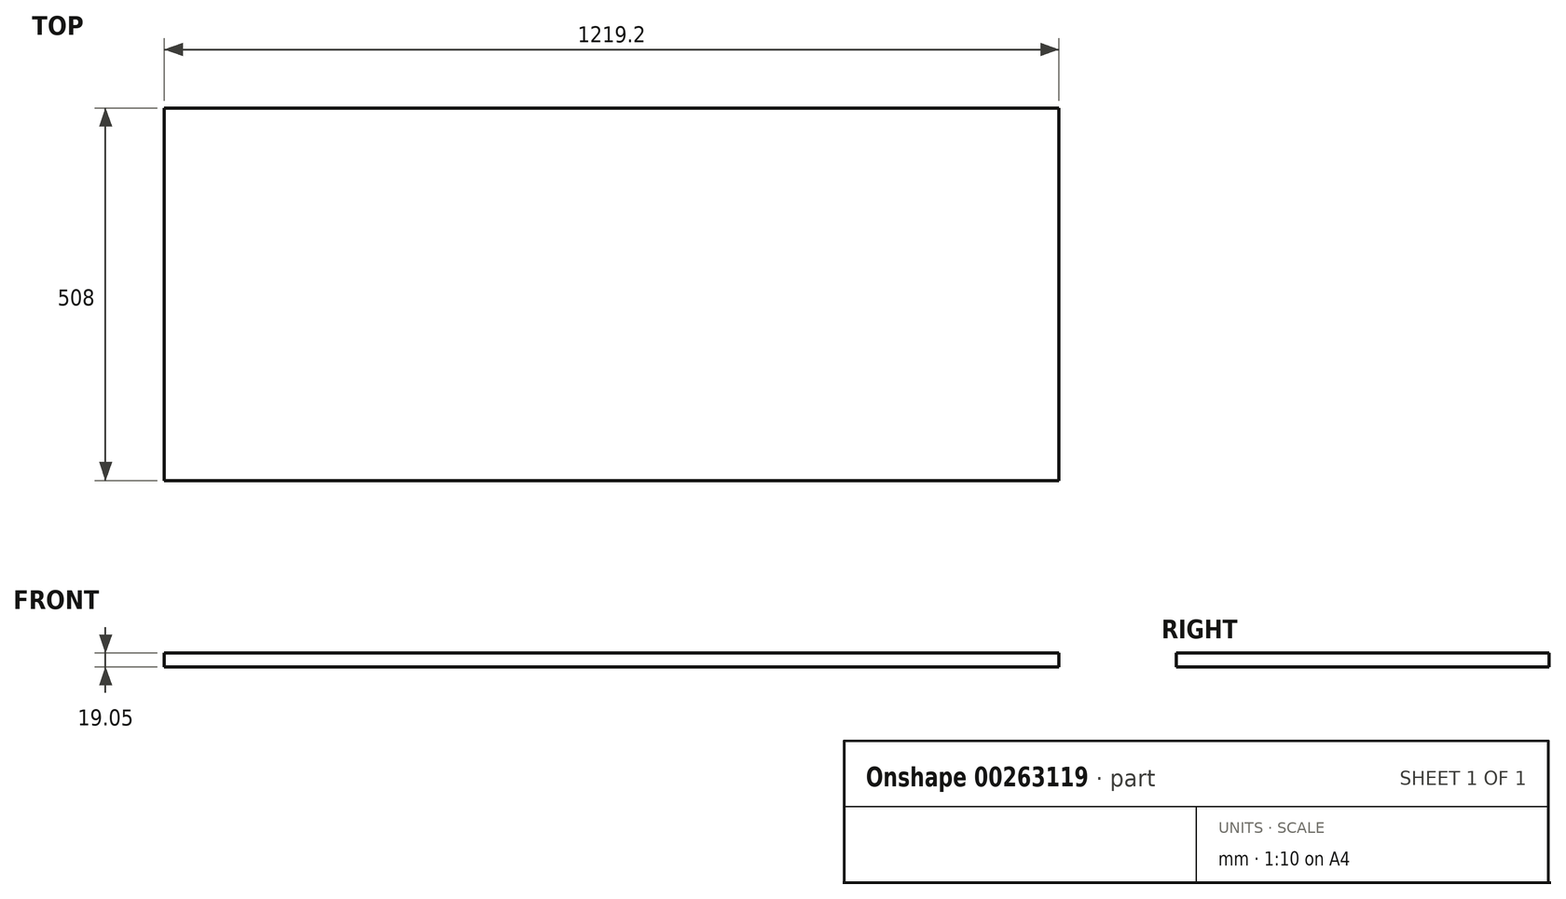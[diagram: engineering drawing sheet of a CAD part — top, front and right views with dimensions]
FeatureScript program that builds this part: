
annotation { "Feature Type Name" : "Feature", "Feature Type Description" : "" }
export const myFeature = defineFeature(function(context is Context, id is Id, definition is map)
    precondition{}
    {
        {
            var Q0;
            Q0=qCreatedBy(makeId("Top.planeOp"),FACE);
            var sketch = newSketch(context, id + "F0", { "sketchPlane" : qUnion([Q0])});
            skLineSegment(sketch, "E0.bottom", {"start": v(609.6, 254) * mm, "end": v(-609.6, 254) * mm});
            skLineSegment(sketch, "E0.top", {"start": v(609.6, -254) * mm, "end": v(-609.6, -254) * mm});
            skLineSegment(sketch, "E0.left", {"start": v(609.6, 254) * mm, "end": v(609.6, -254) * mm});
            skLineSegment(sketch, "E0.right", {"start": v(-609.6, 254) * mm, "end": v(-609.6, -254) * mm});
            skPoint(sketch, "E0.middle", {"position": v(0, 0) * mm});
            skSolve(sketch);
        }
        {
            var Q0;
            Q0=qSketchRegion(id+"F0",true);
            extrude(context, id + "F1", {"entities" : qUnion([Q0]), "depth" : 19.05 * mm});
        }
    });
